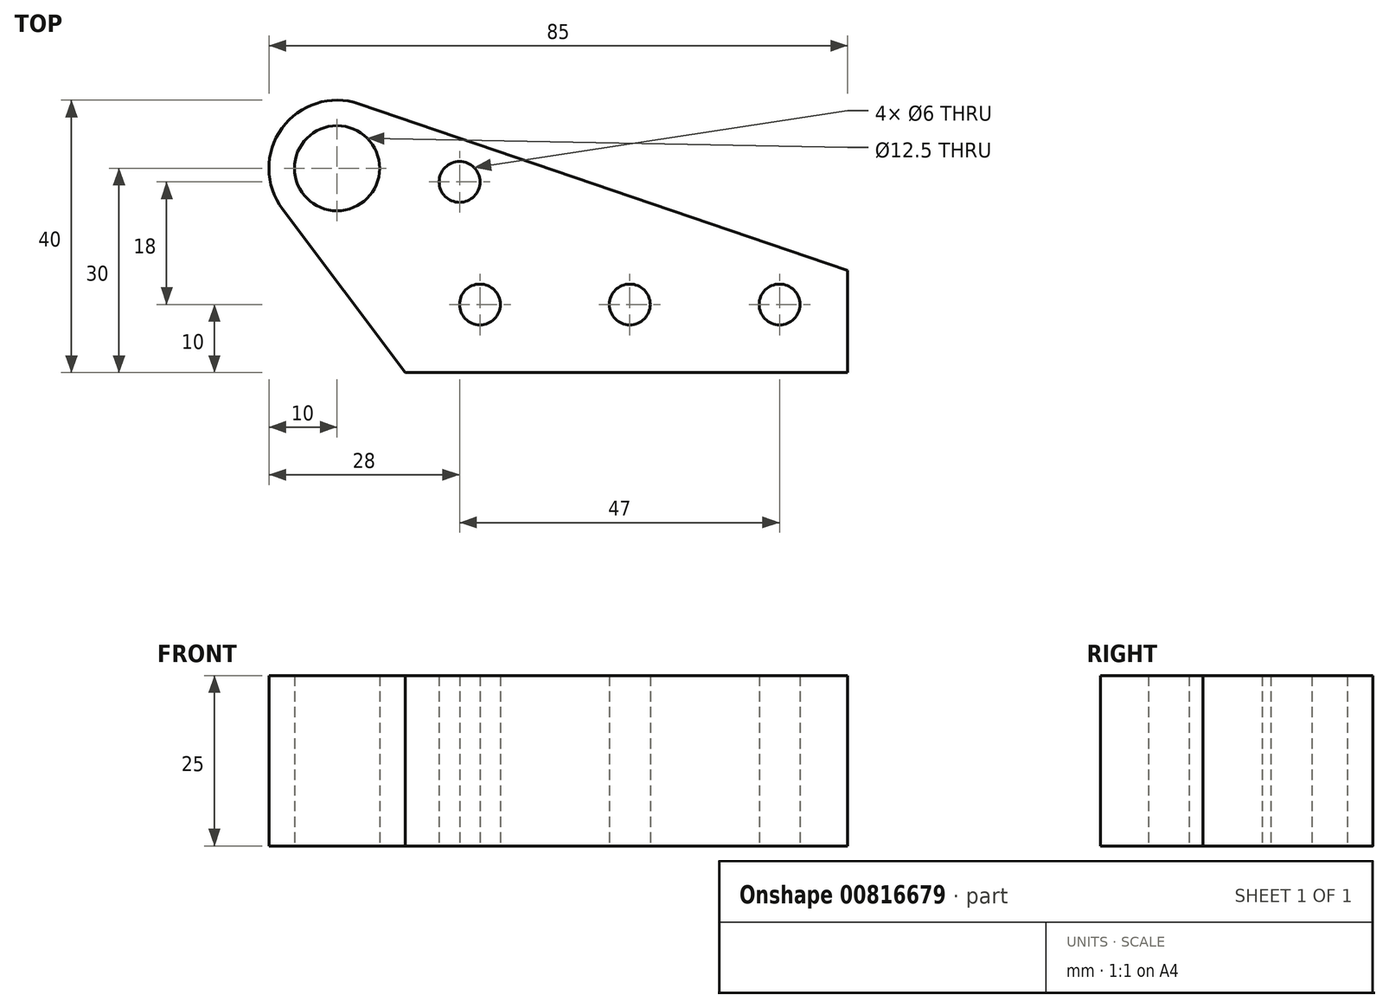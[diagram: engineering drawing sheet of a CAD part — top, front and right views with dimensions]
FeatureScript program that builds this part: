
annotation { "Feature Type Name" : "Feature", "Feature Type Description" : "" }
export const myFeature = defineFeature(function(context is Context, id is Id, definition is map)
    precondition{}
    {
        {
            var Q0;
            Q0=qCreatedBy(makeId("Top.planeOp"),FACE);
            var sketch = newSketch(context, id + "F0", { "sketchPlane" : qUnion([Q0])});
            skCircle(sketch, "E0", {"center": v(0, 0) * mm, "radius": 3 * mm});
            skCircle(sketch, "E1", {"center": v(22, 0) * mm, "radius": 3 * mm});
            skCircle(sketch, "E2", {"center": v(-22, 0) * mm, "radius": 3 * mm});
            skArc(sketch, "E3", {"start": v(-39.77, 29.47) * mm, "mid": v(-51.1, 25.87) * mm, "end": v(-51, 14) * mm});
            skCircle(sketch, "E4", {"center": v(-43, 20) * mm, "radius": 6.25 * mm});
            skLineSegment(sketch, "E5", {"start": v(-33, -10) * mm, "end": v(32, -10) * mm});
            skLineSegment(sketch, "E6", {"start": v(32, -10) * mm, "end": v(32, 5) * mm});
            skLineSegment(sketch, "E7", {"start": v(-51, 14) * mm, "end": v(-33, -10) * mm});
            skCircle(sketch, "E8", {"center": v(-25, 18) * mm, "radius": 3 * mm});
            skLineSegment(sketch, "E9", {"start": v(-39.77, 29.47) * mm, "end": v(32, 5) * mm});
            skSolve(sketch);
        }
        {
            var Q0;
            Q0 = qSketchRegion(id + "F0", true);
            extrude(context, id + "F1", {"entities" : qUnion([Q0]), "depth" : 25 * mm, "offsetDistance" : 25 * mm});
        }
    });
